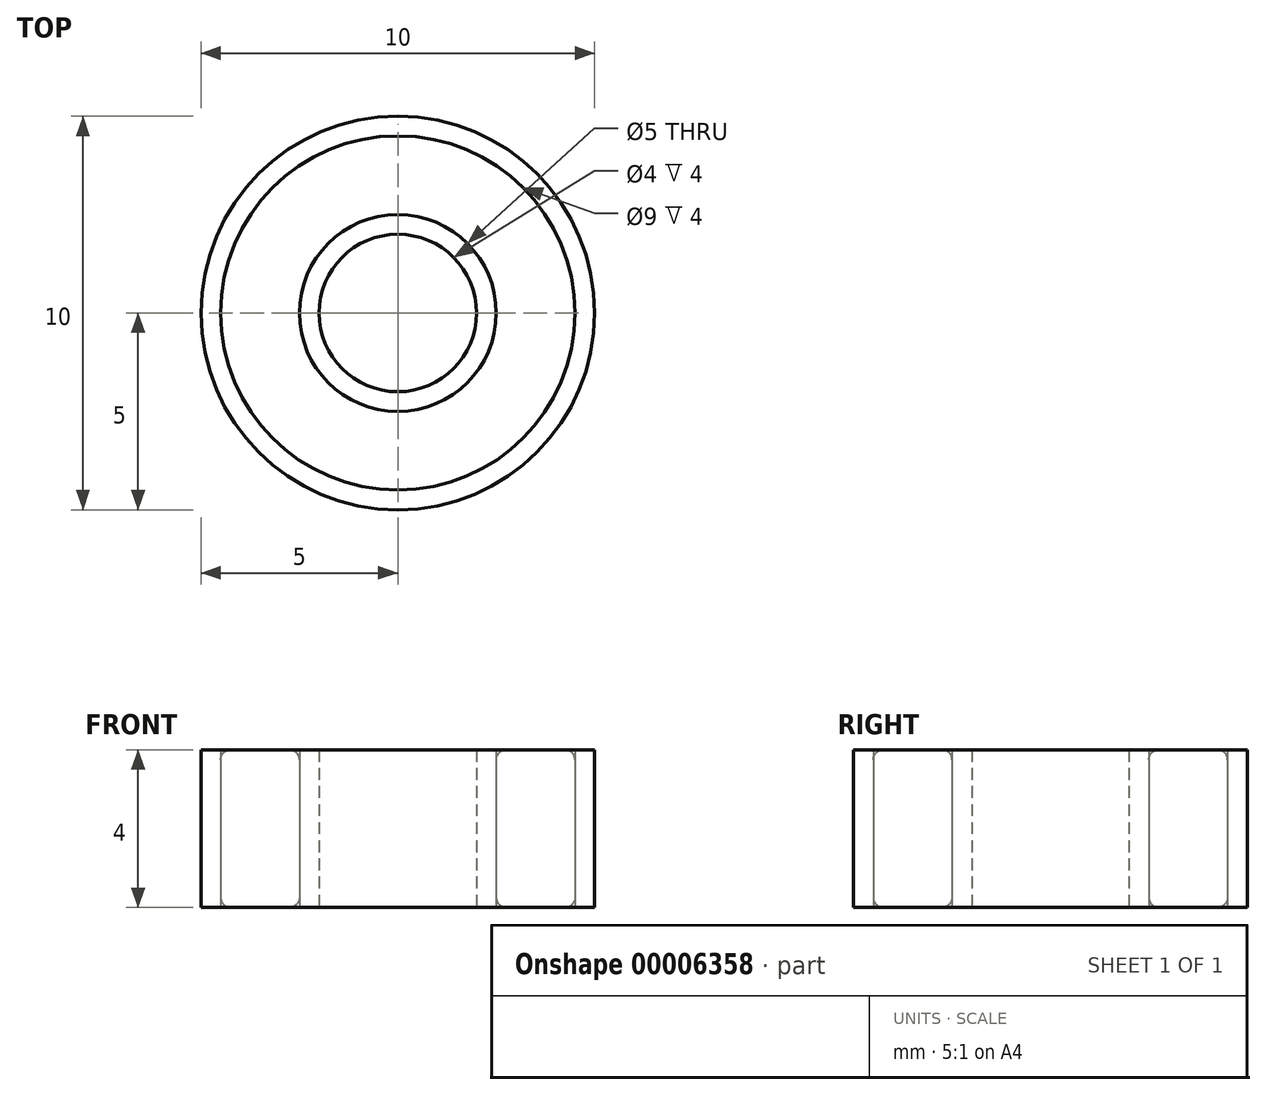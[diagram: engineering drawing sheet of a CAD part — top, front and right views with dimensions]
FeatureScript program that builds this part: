
annotation { "Feature Type Name" : "Feature", "Feature Type Description" : "" }
export const myFeature = defineFeature(function(context is Context, id is Id, definition is map)
    precondition{}
    {
        {
            var Q0;
            Q0=qCreatedBy(makeId("Top.planeOp"),FACE);
            var sketch = newSketch(context, id + "F0", { "sketchPlane" : qUnion([Q0])});
            skCircle(sketch, "E0", {"center": v(0, 0) * mm, "radius": 2 * mm});
            skCircle(sketch, "E1", {"center": v(0, 0) * mm, "radius": 5 * mm});
            skCircle(sketch, "E2.0", {"center": v(0, 0) * mm, "radius": 2.5 * mm});
            skCircle(sketch, "E3.0", {"center": v(0, 0) * mm, "radius": 4.5 * mm});
            skSolve(sketch);
        }
        {
            var Q0;
            Q0=makeQuery(id+"F0.imprint","IMPRINT",FACE,{"disambiguationData":[TD([[makeQuery(id+"F0.imprint","IMPRINT",EDGE,{"derivedFrom":sQuery(id+"F0.wireOp",EDGE,"E0")}),-1.0]])]});
            var Q1;
            Q1=makeQuery(id+"F0.imprint","IMPRINT",FACE,{"disambiguationData":[TD([[makeQuery(id+"F0.imprint","IMPRINT",EDGE,{"derivedFrom":sQuery(id+"F0.wireOp",EDGE,"E1")}),1.0]])]});
            extrude(context, id + "F1", {"entities" : qUnion([Q0, Q1]), "depth" : 4 * mm});
        }
        {
            var Q0;
            Q0=makeQuery(id+"F0.imprint","IMPRINT",FACE,{"disambiguationData":[TD([[makeQuery(id+"F0.imprint","IMPRINT",EDGE,{"derivedFrom":sQuery(id+"F0.wireOp",EDGE,"E2.0")}),-1.0]])]});
            extrude(context, id + "F2", {"entities" : qUnion([Q0]), "depth" : 4 * mm});
        }
        {
            var Q0;
            Q0=makeQuery(id+"F2.opExtrude","CAP_FACE",FACE,{"disambiguationData":[OSD([sQuery(id+"F0.wireOp",EDGE,"E2.0"),sQuery(id+"F0.wireOp",EDGE,"E3.0")])],"isStart":true});
            var Q1;
            Q1=makeQuery(id+"F2.opExtrude","CAP_FACE",FACE,{"disambiguationData":[OSD([sQuery(id+"F0.wireOp",EDGE,"E2.0"),sQuery(id+"F0.wireOp",EDGE,"E3.0")])],"isStart":false});
            fillet(context, id + "F3", {"entities" : qUnion([Q0, Q1]), "radius" : .25 * mm, "tangentPropagation" : true, "allowEdgeOverflow" : false});
        }
    });
